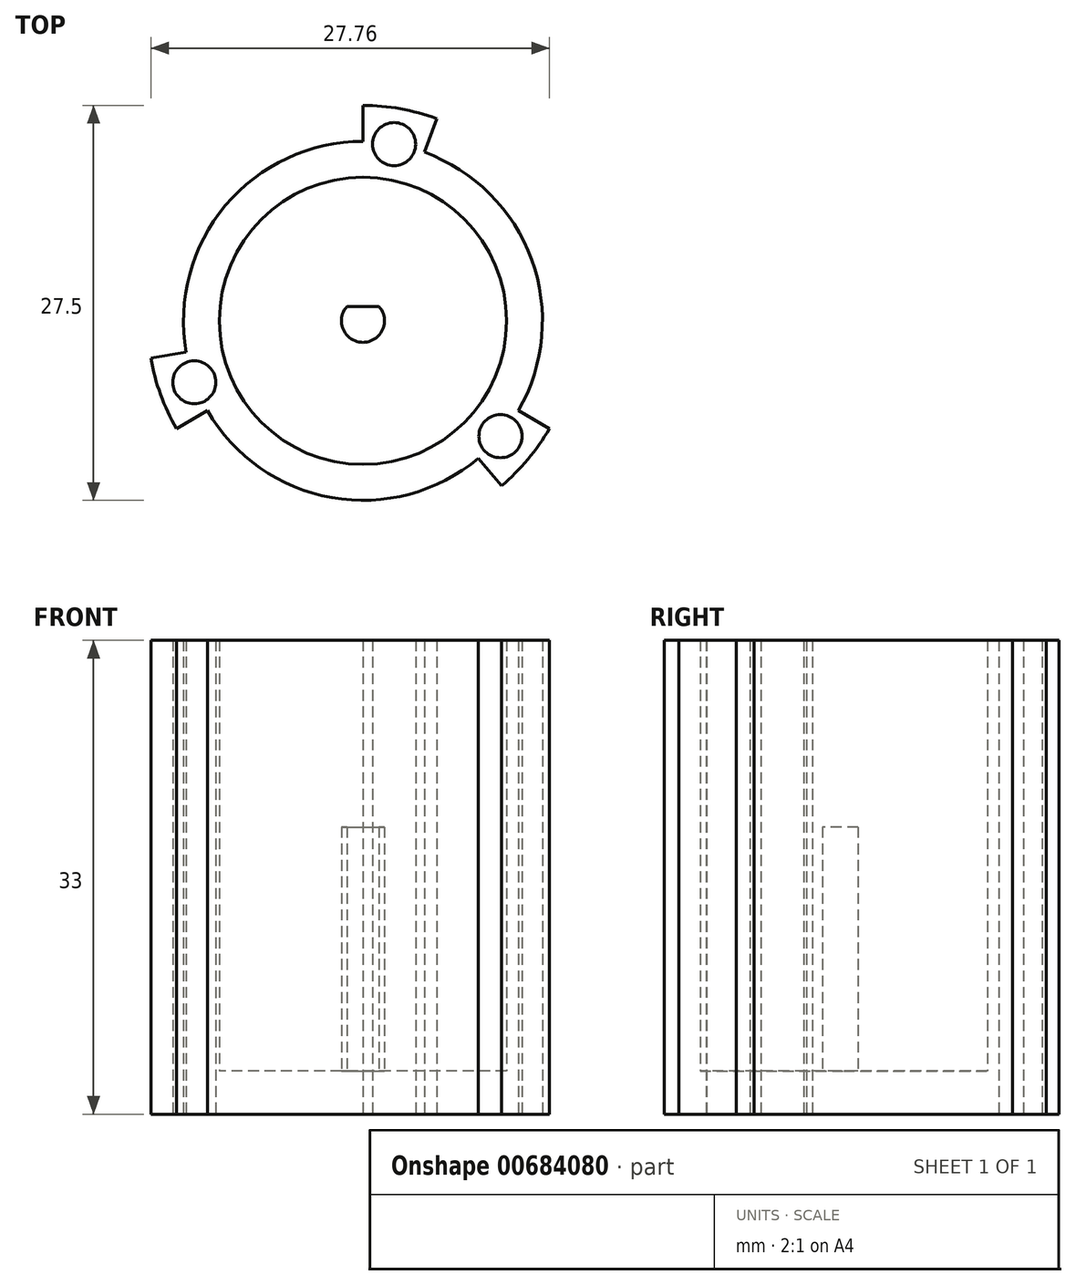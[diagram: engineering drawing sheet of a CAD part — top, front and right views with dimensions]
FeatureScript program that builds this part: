
annotation { "Feature Type Name" : "Feature", "Feature Type Description" : "" }
export const myFeature = defineFeature(function(context is Context, id is Id, definition is map)
    precondition{}
    {
        {
            var Q0;
            Q0=qCreatedBy(makeId("Top.planeOp"),FACE);
            var sketch = newSketch(context, id + "F0", { "sketchPlane" : qUnion([Q0])});
            skCircle(sketch, "E0", {"center": v(0, 0) * mm, "radius": 10 * mm});
            skArc(sketch, "E1.0", {"start": v(-10.83, -6.25) * mm, "mid": v(-2.17, -12.31) * mm, "end": v(8.03, -9.58) * mm});
            skArc(sketch, "E2.0", {"start": v(5.13, 14.1) * mm, "mid": v(2.6, 14.77) * mm, "end": v(0, 15) * mm});
            skLineSegment(sketch, "E3", {"start": v(0, 12.5) * mm, "end": v(0, 15) * mm});
            skLineSegment(sketch, "E4", {"start": v(4.28, 11.75) * mm, "end": v(5.13, 14.1) * mm});
            skArc(sketch, "E5.1.0", {"start": v(-14.77, -2.6) * mm, "mid": v(-14.1, -5.13) * mm, "end": v(-13, -7.5) * mm});
            skLineSegment(sketch, "E5.1.1", {"start": v(-10.83, -6.25) * mm, "end": v(-13, -7.5) * mm});
            skLineSegment(sketch, "E5.1.2", {"start": v(-12.31, -2.17) * mm, "end": v(-14.77, -2.6) * mm});
            skArc(sketch, "E5.2.0", {"start": v(9.64, -11.5) * mm, "mid": v(11.5, -9.64) * mm, "end": v(13, -7.5) * mm});
            skLineSegment(sketch, "E5.2.1", {"start": v(10.83, -6.25) * mm, "end": v(13, -7.5) * mm});
            skLineSegment(sketch, "E5.2.2", {"start": v(8.03, -9.58) * mm, "end": v(9.64, -11.5) * mm});
            skCircle(sketch, "E6", {"center": v(2.17, 12.31) * mm, "radius": 1.5 * mm});
            skCircle(sketch, "E7", {"center": v(9.58, -8.03) * mm, "radius": 1.5 * mm});
            skCircle(sketch, "E8", {"center": v(-11.75, -4.28) * mm, "radius": 1.5 * mm});
            skArc(sketch, "E9.trimOffspring", {"start": v(10.83, -6.25) * mm, "mid": v(11.75, 4.28) * mm, "end": v(4.28, 11.75) * mm});
            skArc(sketch, "E10.trimOffspring", {"start": v(0, 12.5) * mm, "mid": v(-9.58, 8.03) * mm, "end": v(-12.31, -2.17) * mm});
            skArc(sketch, "E11", {"start": v(-1.12, 1) * mm, "mid": v(0, -1.5) * mm, "end": v(1.12, 1) * mm});
            skLineSegment(sketch, "E12", {"start": v(-1.12, 1) * mm, "end": v(1.12, 1) * mm});
            skSolve(sketch);
        }
        {
            var Q0;
            Q0=makeQuery(id+"F0.imprint","IMPRINT",FACE,{"disambiguationData":[TD([[makeQuery(id+"F0.imprint","IMPRINT",EDGE,{"derivedFrom":sQuery(id+"F0.wireOp",EDGE,"E0")}),1.0]])]});
            var Q1;
            Q1=makeQuery(id+"F0.imprint","IMPRINT",FACE,{"disambiguationData":[TD([[makeQuery(id+"F0.imprint","IMPRINT",EDGE,{"derivedFrom":sQuery(id+"F0.wireOp",EDGE,"E0")}),-1.0]])]});
            extrude(context, id + "F1", {"entities" : qUnion([Q0, Q1]), "depth" : 3 * mm, "offsetDistance" : 25 * mm});
        }
        {
            var Q0;
            Q0=makeQuery(id+"F0.imprint","IMPRINT",FACE,{"disambiguationData":[TD([[makeQuery(id+"F0.imprint","IMPRINT",EDGE,{"derivedFrom":sQuery(id+"F0.wireOp",EDGE,"E0")}),-1.0]])]});
            extrude(context, id + "F2", {"entities" : qUnion([Q0]), "operationType" : NewBodyOperationType.ADD, "depth" : 33 * mm, "offsetDistance" : 25 * mm});
        }
        {
            var Q0;
            Q0=makeQuery(id+"F0.imprint","IMPRINT",FACE,{"disambiguationData":[TD([[makeQuery(id+"F0.imprint","IMPRINT",EDGE,{"derivedFrom":sQuery(id+"F0.wireOp",EDGE,"E11")}),1.0]])]});
            extrude(context, id + "F3", {"entities" : qUnion([Q0]), "operationType" : NewBodyOperationType.ADD, "depth" : 20 * mm, "offsetDistance" : 25 * mm});
        }
    });
